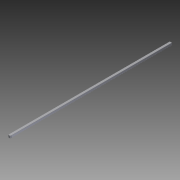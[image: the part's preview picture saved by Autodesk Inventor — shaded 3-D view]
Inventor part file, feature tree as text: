
AUTODESK INVENTOR PART (.ipt)
format: ipt  version: 2014 (Build 180170000, 170)  size: 135,680 bytes
history: native  units: in
note: dims shown in document units (in); Inventor stores cm internally (conversion verified against a paired STEP export)
features: other x1, imported_body x1, extrude x1, sketch x1
ambient origin geometry x8: Origin, YZ Plane, XZ Plane, XY Plane, X Axis, Y Axis, Z Axis, Center Point
bodies: Body1 (feature_tree)
feature tree (4):
  parser-record x1  (decoder bookkeeping rows leaked as tree rows — omitted from the tree; the rows remain in map.json)
  imported_body  "Base1"
  extrude  "Extrusion1"  Depth=1.0in TaperAngle=0.0deg
  sketch  "Sketch1"  dims[d0=3.0in d1=1.0in d2=0.0in]
